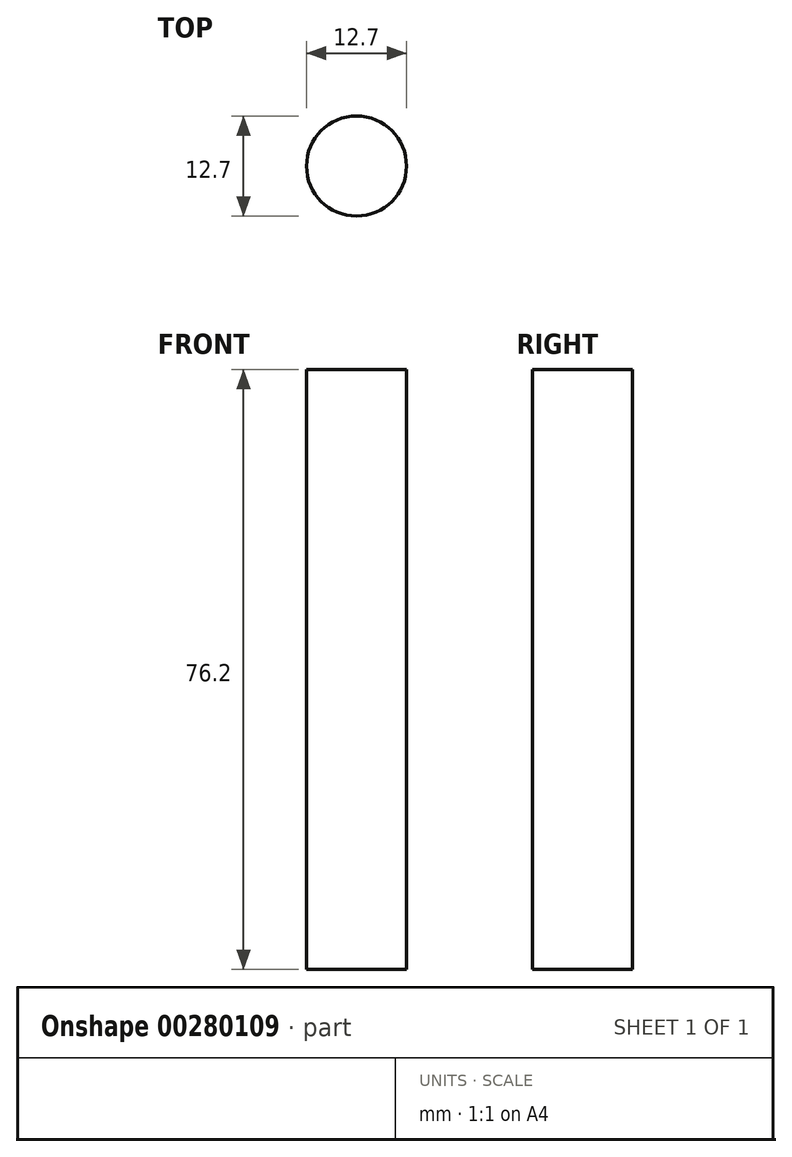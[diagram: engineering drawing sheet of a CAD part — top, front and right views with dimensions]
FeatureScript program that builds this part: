
annotation { "Feature Type Name" : "Feature", "Feature Type Description" : "" }
export const myFeature = defineFeature(function(context is Context, id is Id, definition is map)
    precondition{}
    {
        {
            var Q0;
            Q0=qCreatedBy(makeId("Top.planeOp"),FACE);
            var sketch = newSketch(context, id + "F0", { "sketchPlane" : qUnion([Q0])});
            skCircle(sketch, "E0", {"center": v(0, 0) * mm, "radius": 6.35 * mm});
            skSolve(sketch);
        }
        {
            var Q0;
            Q0 = qSketchRegion(id + "F0", true);
            extrude(context, id + "F1", {"entities" : qUnion([Q0]), "depth" : 76.2 * mm});
        }
    });
